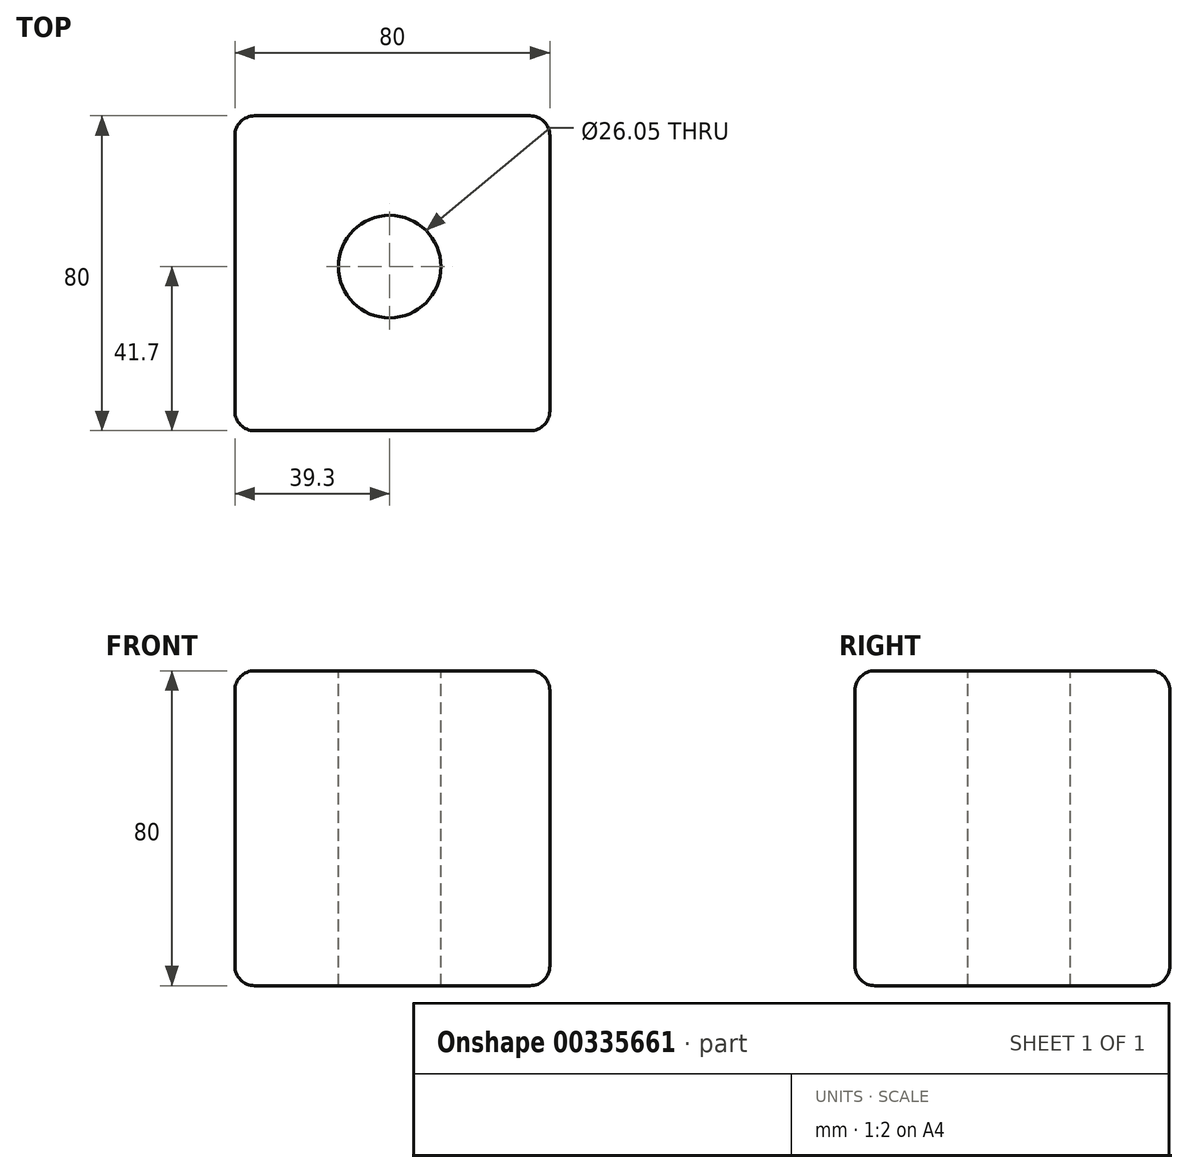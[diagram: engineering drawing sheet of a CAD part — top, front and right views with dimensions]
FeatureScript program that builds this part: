
annotation { "Feature Type Name" : "Feature", "Feature Type Description" : "" }
export const myFeature = defineFeature(function(context is Context, id is Id, definition is map)
    precondition{}
    {
        {
            var Q0;
            Q0=qCreatedBy(makeId("Top.planeOp"),FACE);
            var sketch = newSketch(context, id + "F0", { "sketchPlane" : qUnion([Q0])});
            skLineSegment(sketch, "E0.bottom", {"start": v(-32.4, 30.05) * mm, "end": v(47.6, 30.05) * mm});
            skLineSegment(sketch, "E0.top", {"start": v(-32.4, -49.95) * mm, "end": v(47.6, -49.95) * mm});
            skLineSegment(sketch, "E0.left", {"start": v(-32.4, 30.05) * mm, "end": v(-32.4, -49.95) * mm});
            skLineSegment(sketch, "E0.right", {"start": v(47.6, 30.05) * mm, "end": v(47.6, -49.95) * mm});
            skPoint(sketch, "E0.middle", {"position": v(7.6, -9.95) * mm});
            skSolve(sketch);
        }
        {
            var Q0;
            Q0=makeQuery(id+"F0.imprint","IMPRINT",FACE,{"disambiguationData":[TD([[makeQuery(id+"F0.imprint","IMPRINT",EDGE,{"derivedFrom":sQuery(id+"F0.wireOp",EDGE,"E0.bottom")}),-1.0]])]});
            extrude(context, id + "F1", {"entities" : qUnion([Q0]), "endBound" : BoundingType.SYMMETRIC, "depth" : 80 * mm});
        }
        {
            var Q0;
            Q0=makeQuery(id+"F1.opExtrude","SWEPT_FACE",FACE,{"disambiguationData":[OSD([sQuery(id+"F0.wireOp",EDGE,"E0.top")])]});
            var Q1;
            Q1=makeQuery(id+"F1.opExtrude","SWEPT_FACE",FACE,{"disambiguationData":[OSD([sQuery(id+"F0.wireOp",EDGE,"E0.left")])]});
            var Q2;
            Q2=makeQuery(id+"F1.opExtrude","SWEPT_FACE",FACE,{"disambiguationData":[OSD([sQuery(id+"F0.wireOp",EDGE,"E0.bottom")])]});
            var Q3;
            Q3=makeQuery(id+"F1.opExtrude","SWEPT_FACE",FACE,{"disambiguationData":[OSD([sQuery(id+"F0.wireOp",EDGE,"E0.right")])]});
            fillet(context, id + "F2", {"entities" : qUnion([Q0, Q1, Q2, Q3]), "radius" : 5 * mm, "tangentPropagation" : true, "allowEdgeOverflow" : false});
        }
        {
            var Q0;
            Q0=makeQuery(id+"F1.opExtrude","CAP_FACE",FACE,{"disambiguationData":[OSD([sQuery(id+"F0.wireOp",EDGE,"E0.bottom"),sQuery(id+"F0.wireOp",EDGE,"E0.top"),sQuery(id+"F0.wireOp",EDGE,"E0.left"),sQuery(id+"F0.wireOp",EDGE,"E0.right")])],"isStart":false});
            var sketch = newSketch(context, id + "F3", { "sketchPlane" : qUnion([Q0])});
            skCircle(sketch, "E1", {"center": v(6.9, -8.25) * mm, "radius": 13.02 * mm});
            skSolve(sketch);
        }
        {
            var Q0;
            Q0=makeQuery(id+"F3.imprint","IMPRINT",FACE,{"disambiguationData":[TD([[makeQuery(id+"F3.imprint","IMPRINT",EDGE,{"derivedFrom":sQuery(id+"F3.wireOp",EDGE,"E1")}),1.0]])]});
            extrude(context, id + "F4", {"entities" : qUnion([Q0]), "operationType" : NewBodyOperationType.ADD, "endBound" : BoundingType.THROUGH_ALL, "depth" : 25 * mm});
        }
        {
            var Q0;
            Q0=makeQuery(id+"F4.opExtrude","CAP_FACE",FACE,{"disambiguationData":[OSD([sQuery(id+"F3.wireOp",EDGE,"E1")])],"isStart":false});
            var sketch = newSketch(context, id + "F5", { "sketchPlane" : qUnion([Q0])});
            skSolve(sketch);
        }
        {
            var Q0;
            Q0=makeQuery(id+"F5.imprint","IMPRINT",FACE,{"disambiguationData":[TD([[makeQuery(id+"F5.imprint","IMPRINT",EDGE,{"derivedFrom":makeQuery(id+"F4.opExtrude","CAP_EDGE",EDGE,{"disambiguationData":[OSD([sQuery(id+"F3.wireOp",EDGE,"E1")])],"isStart":false})}),1.0]])]});
            extrude(context, id + "F6", {"entities" : qUnion([Q0]), "operationType" : NewBodyOperationType.REMOVE, "endBound" : BoundingType.THROUGH_ALL, "oppositeDirection" : true, "depth" : 25 * mm});
        }
    });
